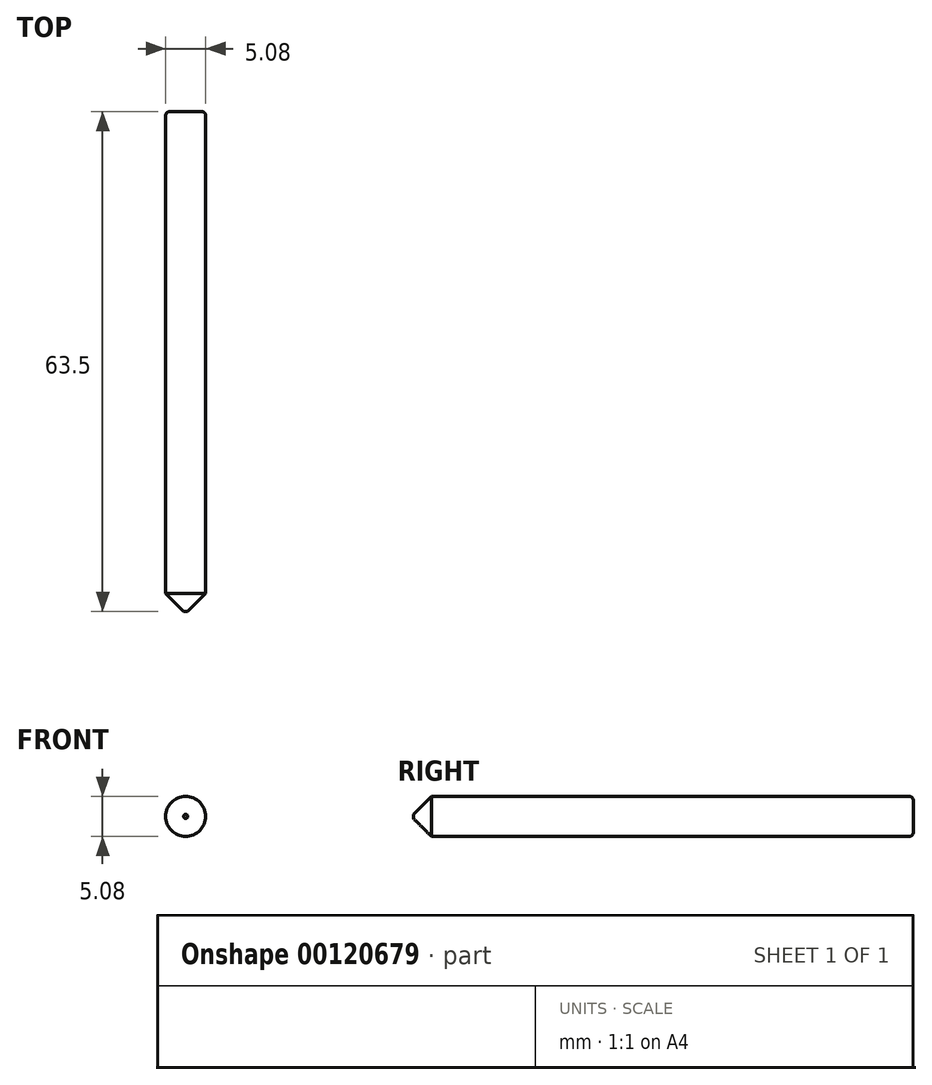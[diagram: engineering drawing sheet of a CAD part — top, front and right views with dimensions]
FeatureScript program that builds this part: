
annotation { "Feature Type Name" : "Feature", "Feature Type Description" : "" }
export const myFeature = defineFeature(function(context is Context, id is Id, definition is map)
    precondition{}
    {
        {
            var Q0;
            Q0=qCreatedBy(makeId("Front.planeOp"),FACE);
            var sketch = newSketch(context, id + "F0", { "sketchPlane" : qUnion([Q0])});
            skCircle(sketch, "E0", {"center": v(-11.58, 5.6) * mm, "radius": 2.54 * mm});
            skSolve(sketch);
        }
        {
            var Q0;
            Q0=makeQuery(id+"F0.imprint","IMPRINT",FACE,{"disambiguationData":[TD([[makeQuery(id+"F0.imprint","IMPRINT",EDGE,{"derivedFrom":sQuery(id+"F0.wireOp",EDGE,"E0")}),1.0]])]});
            extrude(context, id + "F1", {"entities" : qUnion([Q0]), "depth" : 63.5 * mm});
        }
        {
            var Q0;
            Q0=makeQuery(id+"F1.opExtrude","CAP_EDGE",EDGE,{"disambiguationData":[OSD([sQuery(id+"F0.wireOp",EDGE,"E0")])],"isStart":true});
            fillet(context, id + "F2", {"entities" : qUnion([Q0]), "radius" : 0.5 * mm, "tangentPropagation" : true, "allowEdgeOverflow" : false});
        }
        {
            var Q0;
            Q0=makeQuery(id+"F1.opExtrude","CAP_EDGE",EDGE,{"disambiguationData":[OSD([sQuery(id+"F0.wireOp",EDGE,"E0")])],"isStart":false});
            chamfer(context, id + "F3", {"entities" : qUnion([Q0]), "width" : 2.3 * mm, "tangentPropagation" : true});
        }
    });
